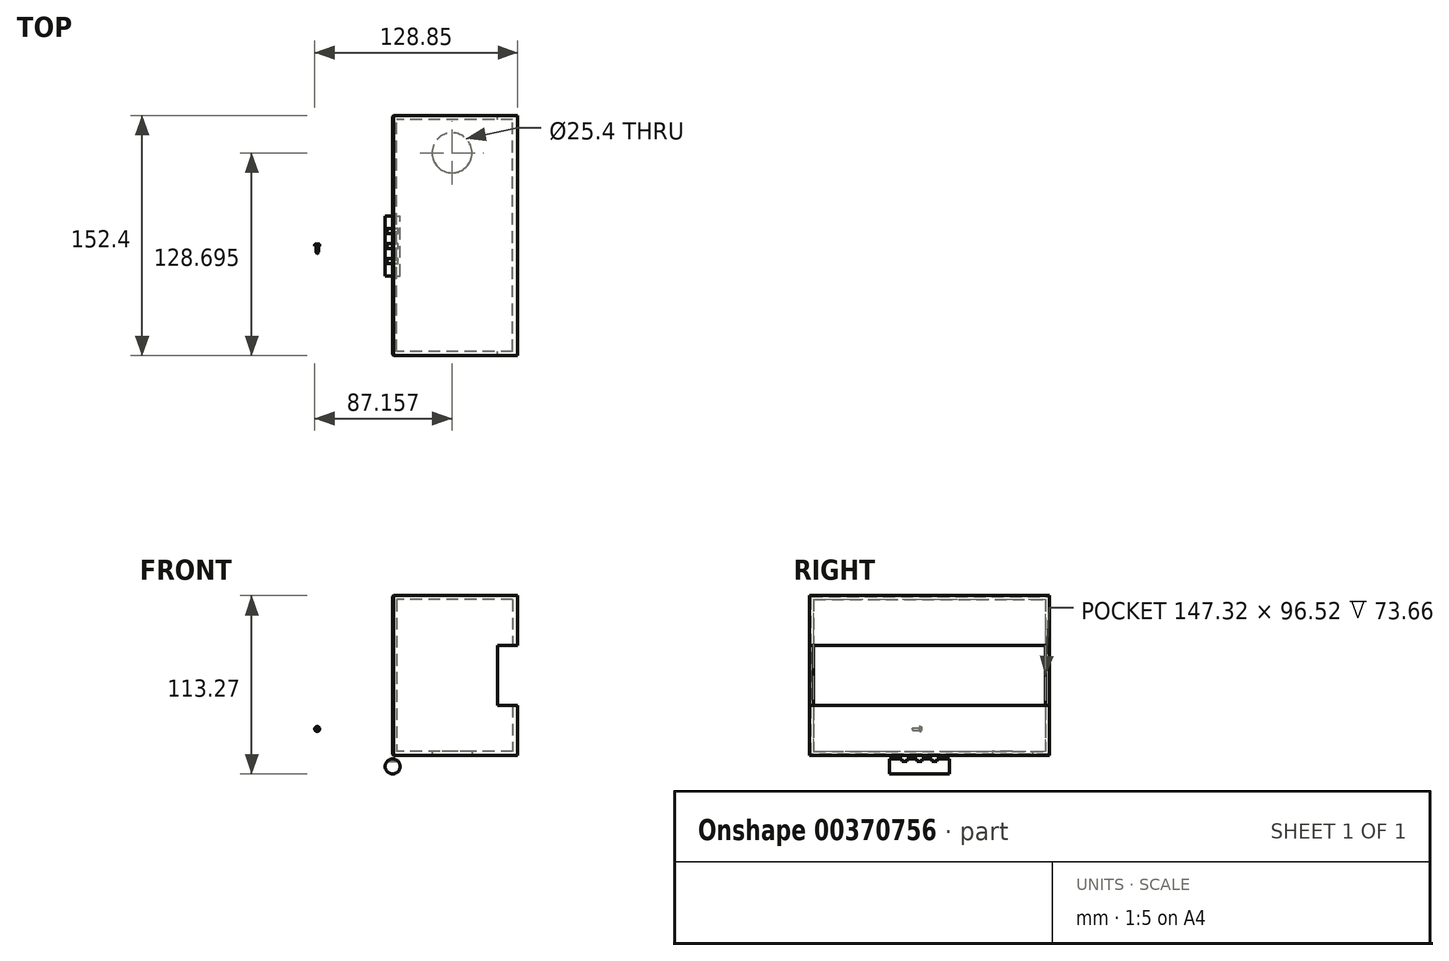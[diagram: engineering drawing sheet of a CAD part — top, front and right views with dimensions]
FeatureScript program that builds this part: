
annotation { "Feature Type Name" : "Feature", "Feature Type Description" : "" }
export const myFeature = defineFeature(function(context is Context, id is Id, definition is map)
    precondition{}
    {
        {
            var Q0;
            Q0=qCreatedBy(makeId("Front.planeOp"),FACE);
            var sketch = newSketch(context, id + "F0", { "sketchPlane" : qUnion([Q0])});
            skCircle(sketch, "E0", {"center": v(0, 0) * mm, "radius": 4.76 * mm});
            skSolve(sketch);
        }
        {
            var Q0;
            Q0 = qSketchRegion(id + "F0", true);
            extrude(context, id + "F1", {"entities" : qUnion([Q0]), "endBound" : BoundingType.SYMMETRIC, "depth" : 38.1 * mm});
        }
        {
            var Q0;
            Q0=qCreatedBy(makeId("Right.planeOp"),FACE);
            var sketch = newSketch(context, id + "F2", { "sketchPlane" : qUnion([Q0])});
            skLineSegment(sketch, "E1.bottom", {"start": v(-1.59, 6.48) * mm, "end": v(1.59, 6.48) * mm});
            skLineSegment(sketch, "E1.top", {"start": v(-1.59, 3.18) * mm, "end": v(1.59, 3.18) * mm});
            skLineSegment(sketch, "E1.left", {"start": v(-1.59, 6.48) * mm, "end": v(-1.59, 3.18) * mm});
            skLineSegment(sketch, "E1.right", {"start": v(1.59, 6.48) * mm, "end": v(1.59, 3.18) * mm});
            skLineSegment(sketch, "E2.bottom", {"start": v(7.94, 6.48) * mm, "end": v(11.11, 6.48) * mm});
            skLineSegment(sketch, "E2.top", {"start": v(7.94, 3.17) * mm, "end": v(11.11, 3.18) * mm});
            skLineSegment(sketch, "E2.left", {"start": v(7.94, 6.48) * mm, "end": v(7.94, 3.17) * mm});
            skLineSegment(sketch, "E2.right", {"start": v(11.11, 6.48) * mm, "end": v(11.11, 3.18) * mm});
            skLineSegment(sketch, "E3.MirrorCS", {"start": v(-7.94, 6.48) * mm, "end": v(-11.11, 6.48) * mm});
            skLineSegment(sketch, "E4.MirrorCS", {"start": v(-11.11, 6.48) * mm, "end": v(-11.11, 3.18) * mm});
            skLineSegment(sketch, "E5.MirrorCS", {"start": v(-7.94, 3.17) * mm, "end": v(-11.11, 3.18) * mm});
            skLineSegment(sketch, "E6.MirrorCS", {"start": v(-7.94, 6.48) * mm, "end": v(-7.94, 3.17) * mm});
            skSolve(sketch);
        }
        {
            var Q0;
            Q0 = qSketchRegion(id + "F2", true);
            extrude(context, id + "F3", {"entities" : qUnion([Q0]), "operationType" : NewBodyOperationType.REMOVE, "endBound" : BoundingType.SYMMETRIC, "oppositeDirection" : true, "depth" : 25.4 * mm});
        }
        {
            var Q0;
            Q0=qCreatedBy(makeId("Right.planeOp"),FACE);
            var sketch = newSketch(context, id + "F4", { "sketchPlane" : qUnion([Q0])});
            skLineSegment(sketch, "E7.bottom", {"start": v(-69.66, 108.51) * mm, "end": v(82.74, 108.51) * mm});
            skLineSegment(sketch, "E7.top", {"start": v(-69.66, 6.91) * mm, "end": v(82.74, 6.91) * mm});
            skLineSegment(sketch, "E7.left", {"start": v(-69.66, 108.51) * mm, "end": v(-69.66, 6.91) * mm});
            skLineSegment(sketch, "E7.right", {"start": v(82.74, 108.51) * mm, "end": v(82.74, 6.91) * mm});
            skSolve(sketch);
        }
        {
            var Q0;
            Q0 = qSketchRegion(id + "F4", true);
            extrude(context, id + "F5", {"entities" : qUnion([Q0]), "depth" : 76.2 * mm});
        }
        {
            var Q0;
            Q0=makeQuery(id+"F5.opExtrude","CAP_FACE",FACE,{"disambiguationData":[OSD([sQuery(id+"F4.wireOp",EDGE,"E7.bottom"),sQuery(id+"F4.wireOp",EDGE,"E7.top"),sQuery(id+"F4.wireOp",EDGE,"E7.left"),sQuery(id+"F4.wireOp",EDGE,"E7.right")])],"isStart":false});
            shell(context, id + "F6", {"entities" : qUnion([Q0]), "thickness" : 2.54 * mm});
        }
        {
            var Q0;
            Q0=makeQuery(id+"F5.opExtrude","CAP_FACE",FACE,{"disambiguationData":[OSD([sQuery(id+"F4.wireOp",EDGE,"E7.bottom"),sQuery(id+"F4.wireOp",EDGE,"E7.top"),sQuery(id+"F4.wireOp",EDGE,"E7.left"),sQuery(id+"F4.wireOp",EDGE,"E7.right")])],"isStart":false});
            var sketch = newSketch(context, id + "F7", { "sketchPlane" : qUnion([Q0])});
            skLineSegment(sketch, "E8.bottom", {"start": v(-69.66, 108.51) * mm, "end": v(82.74, 108.51) * mm});
            skLineSegment(sketch, "E8.top", {"start": v(-69.66, 6.91) * mm, "end": v(82.74, 6.91) * mm});
            skLineSegment(sketch, "E8.left", {"start": v(-69.66, 108.51) * mm, "end": v(-69.66, 6.91) * mm});
            skLineSegment(sketch, "E8.right", {"start": v(82.74, 108.51) * mm, "end": v(82.74, 6.91) * mm});
            skSolve(sketch);
        }
        {
            var Q0;
            Q0 = qSketchRegion(id + "F7", true);
            extrude(context, id + "F8", {"entities" : qUnion([Q0]), "operationType" : NewBodyOperationType.ADD, "depth" : 3.17 * mm});
        }
        {
            var Q0;
            Q0=makeQuery(id+"F8.opExtrude","CAP_FACE",FACE,{"disambiguationData":[OSD([sQuery(id+"F7.wireOp",EDGE,"E8.bottom"),sQuery(id+"F7.wireOp",EDGE,"E8.top"),sQuery(id+"F7.wireOp",EDGE,"E8.left"),sQuery(id+"F7.wireOp",EDGE,"E8.right")])],"isStart":false});
            var sketch = newSketch(context, id + "F9", { "sketchPlane" : qUnion([Q0])});
            skLineSegment(sketch, "E9.bottom", {"start": v(-82.06, 76.76) * mm, "end": v(95.74, 76.76) * mm});
            skLineSegment(sketch, "E9.top", {"start": v(-82.06, 38.66) * mm, "end": v(95.74, 38.66) * mm});
            skLineSegment(sketch, "E9.left", {"start": v(-82.06, 76.76) * mm, "end": v(-82.06, 38.66) * mm});
            skLineSegment(sketch, "E9.right", {"start": v(95.74, 76.76) * mm, "end": v(95.74, 38.66) * mm});
            skLineSegment(sketch, "E10", {"start": v(-69.66, 57.71) * mm, "end": v(82.74, 57.71) * mm, "construction": true});
            skSolve(sketch);
        }
        {
            var Q0;
            Q0 = qSketchRegion(id + "F9", true);
            extrude(context, id + "F10", {"entities" : qUnion([Q0]), "operationType" : NewBodyOperationType.REMOVE, "oppositeDirection" : true, "depth" : 12.7 * mm});
        }
        {
            var Q0;
            Q0=makeQuery(id+"F8.boolean.opBoolean","MERGE",FACE,{"derivedFrom":[makeQuery(id+"F5.opExtrude","SWEPT_FACE",FACE,{"disambiguationData":[OSD([sQuery(id+"F4.wireOp",EDGE,"E7.top")])]}),makeQuery(id+"F8.opExtrude","SWEPT_FACE",FACE,{"disambiguationData":[OSD([sQuery(id+"F7.wireOp",EDGE,"E8.top")])]})]});
            var sketch = newSketch(context, id + "F11", { "sketchPlane" : qUnion([Q0])});
            skCircle(sketch, "E11", {"center": v(37.69, -59.03) * mm, "radius": 12.7 * mm});
            skSolve(sketch);
        }
        {
            var Q0;
            Q0 = qSketchRegion(id + "F11", true);
            extrude(context, id + "F12", {"entities" : qUnion([Q0]), "operationType" : NewBodyOperationType.REMOVE, "oppositeDirection" : true, "depth" : 25.4 * mm});
        }
        {
            var Q0;
            Q0=qCreatedBy(makeId("Front.planeOp"),FACE);
            var sketch = newSketch(context, id + "F13", { "sketchPlane" : qUnion([Q0])});
            skCircle(sketch, "E12", {"center": v(-47.88, 23.8) * mm, "radius": 0.8 * mm});
            skSolve(sketch);
        }
        {
            var Q0;
            Q0 = qSketchRegion(id + "F13", true);
            extrude(context, id + "F14", {"entities" : qUnion([Q0]), "depth" : 4.76 * mm});
        }
        {
            var Q0;
            Q0=makeQuery(id+"F14.opExtrude","CAP_EDGE",EDGE,{"disambiguationData":[OSD([sQuery(id+"F13.wireOp",EDGE,"E12")])],"isStart":false});
            var Q1;
            Q1=makeQuery(id+"F5.opExtrude","CAP_FACE",FACE,{"disambiguationData":[OSD([sQuery(id+"F4.wireOp",EDGE,"E7.bottom"),sQuery(id+"F4.wireOp",EDGE,"E7.top"),sQuery(id+"F4.wireOp",EDGE,"E7.left"),sQuery(id+"F4.wireOp",EDGE,"E7.right")])],"isStart":true});
            chamfer(context, id + "F15", {"entities" : qUnion([Q0, Q1]), "width" : 0.69 * mm, "tangentPropagation" : true});
        }
        {
            var Q0;
            Q0=makeQuery(id+"F14.opExtrude","CAP_FACE",FACE,{"disambiguationData":[OSD([sQuery(id+"F13.wireOp",EDGE,"E12")])],"isStart":true});
            var sketch = newSketch(context, id + "F16", { "sketchPlane" : qUnion([Q0])});
            skCircle(sketch, "E13", {"center": v(47.88, 23.8) * mm, "radius": 1.59 * mm});
            skSolve(sketch);
        }
        {
            var Q0;
            Q0 = qSketchRegion(id + "F16", true);
            extrude(context, id + "F17", {"entities" : qUnion([Q0]), "operationType" : NewBodyOperationType.ADD, "depth" : 1.27 * mm});
        }
        {
            var Q0;
            Q0=makeQuery(id+"F17.opExtrude","CAP_EDGE",EDGE,{"disambiguationData":[OSD([sQuery(id+"F16.wireOp",EDGE,"E13")])],"isStart":false});
            fillet(context, id + "F18", {"entities" : qUnion([Q0]), "radius" : 0.76 * mm, "tangentPropagation" : true, "allowEdgeOverflow" : false});
        }
        {
            var Q0;
            Q0=makeQuery(id+"F17.opExtrude","CAP_FACE",FACE,{"disambiguationData":[OSD([sQuery(id+"F16.wireOp",EDGE,"E13")])],"isStart":false});
            var sketch = newSketch(context, id + "F19", { "sketchPlane" : qUnion([Q0])});
            skLineSegment(sketch, "E14.bottom", {"start": v(47.76, 24.36) * mm, "end": v(47.98, 24.36) * mm});
            skLineSegment(sketch, "E14.top", {"start": v(47.76, 23.19) * mm, "end": v(47.98, 23.19) * mm});
            skLineSegment(sketch, "E14.left", {"start": v(47.76, 24.36) * mm, "end": v(47.76, 23.19) * mm});
            skLineSegment(sketch, "E14.right", {"start": v(47.98, 24.36) * mm, "end": v(47.98, 23.19) * mm});
            skSolve(sketch);
        }
        {
            var Q0;
            Q0 = qSketchRegion(id + "F19", true);
            extrude(context, id + "F20", {"entities" : qUnion([Q0]), "operationType" : NewBodyOperationType.REMOVE, "oppositeDirection" : true, "depth" : 0.76 * mm});
        }
        {
            var Q0;
            {var subQ0=sQuery(id+"F16.wireOp",EDGE,"E13");Q0=makeQuery(id+"F20.boolean.opBoolean","SPLIT",FACE,{"disambiguationData":[TD([makeQuery(id+"F20.opExtrude","SWEPT_FACE",FACE,{"disambiguationData":[OSD([sQuery(id+"F19.wireOp",EDGE,"E14.right")])]})])],"derivedFrom":makeQuery(id+"F17.opExtrude","CAP_FACE",FACE,{"disambiguationData":[OSD([subQ0])],"isStart":false})});}
            var sketch = newSketch(context, id + "F21", { "sketchPlane" : qUnion([Q0])});
            skLineSegment(sketch, "E15.bottom", {"start": v(47.45, 23.88) * mm, "end": v(48.3, 23.88) * mm});
            skLineSegment(sketch, "E15.top", {"start": v(47.45, 23.67) * mm, "end": v(48.3, 23.67) * mm});
            skLineSegment(sketch, "E15.left", {"start": v(47.45, 23.88) * mm, "end": v(47.45, 23.67) * mm});
            skLineSegment(sketch, "E15.right", {"start": v(48.3, 23.88) * mm, "end": v(48.3, 23.67) * mm});
            skSolve(sketch);
        }
        {
            var Q0;
            Q0 = qSketchRegion(id + "F21", true);
            extrude(context, id + "F22", {"entities" : qUnion([Q0]), "operationType" : NewBodyOperationType.REMOVE, "oppositeDirection" : true, "depth" : 0.76 * mm});
        }
    });
